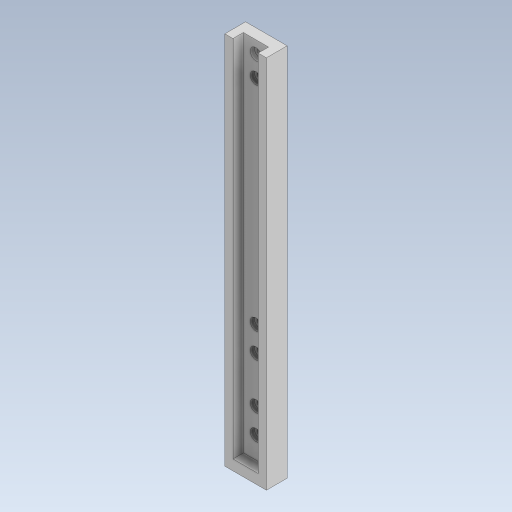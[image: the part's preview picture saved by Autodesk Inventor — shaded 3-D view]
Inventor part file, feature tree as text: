
AUTODESK INVENTOR PART (.ipt)
format: ipt  version: 2023.5 (Build 275446000, 446)  size: 339,968 bytes
history: native  units: in
note: dims shown in document units (in); Inventor stores cm internally (conversion verified against a paired STEP export)
features: extrude x7, sketch x5
ambient origin geometry x8: Origin, YZ Plane, XZ Plane, XY Plane, X Axis, Y Axis, Z Axis, Center Point
bodies: Solid1 (feature_tree)
feature tree (12):
  extrude  "Extrusion1"  Depth=0.3937in
  extrude  "Extrusion2"  Depth=0.4764in
  sketch  "Sketch3"  dims[d5=5.7087in d6=0.0in d7=0.1181in]
  extrude  "Extrusion3"  Depth=0.1181in
  extrude  "Extrusion4"  Depth=0.4134in
  extrude  "Extrusion5"  Depth=0.0787in
  sketch  "Sketch6"  dims[d10=0.1181in d11=0.4724in d12=0.2165in d13=0.2165in d14=0.1969in d15=0.0in d16=0.0787in d17=0.0in d18=1.1811in d19=0.0in d24=0.1181in d25=0.1181in d26=0.2362in d27=0.3937in d28=0.2165in d29=0.2165in d30=0.1969in d31=0.0in d32=0.0787in d33=0.0in d34=0.4331in]
  extrude  "Extrusion6"  Depth=0.0787in
  extrude  "Extrusion7"  Depth=0.0787in
  sketch  "Sketch1"  dims[d0=5.9055in d1=0.3937in]
  sketch  "Sketch2"  dims[d2=0.7874in d3=0.0in d4=0.4764in]
  sketch  "Sketch4"  dims[d8=0.2382in d9=0.4134in]
